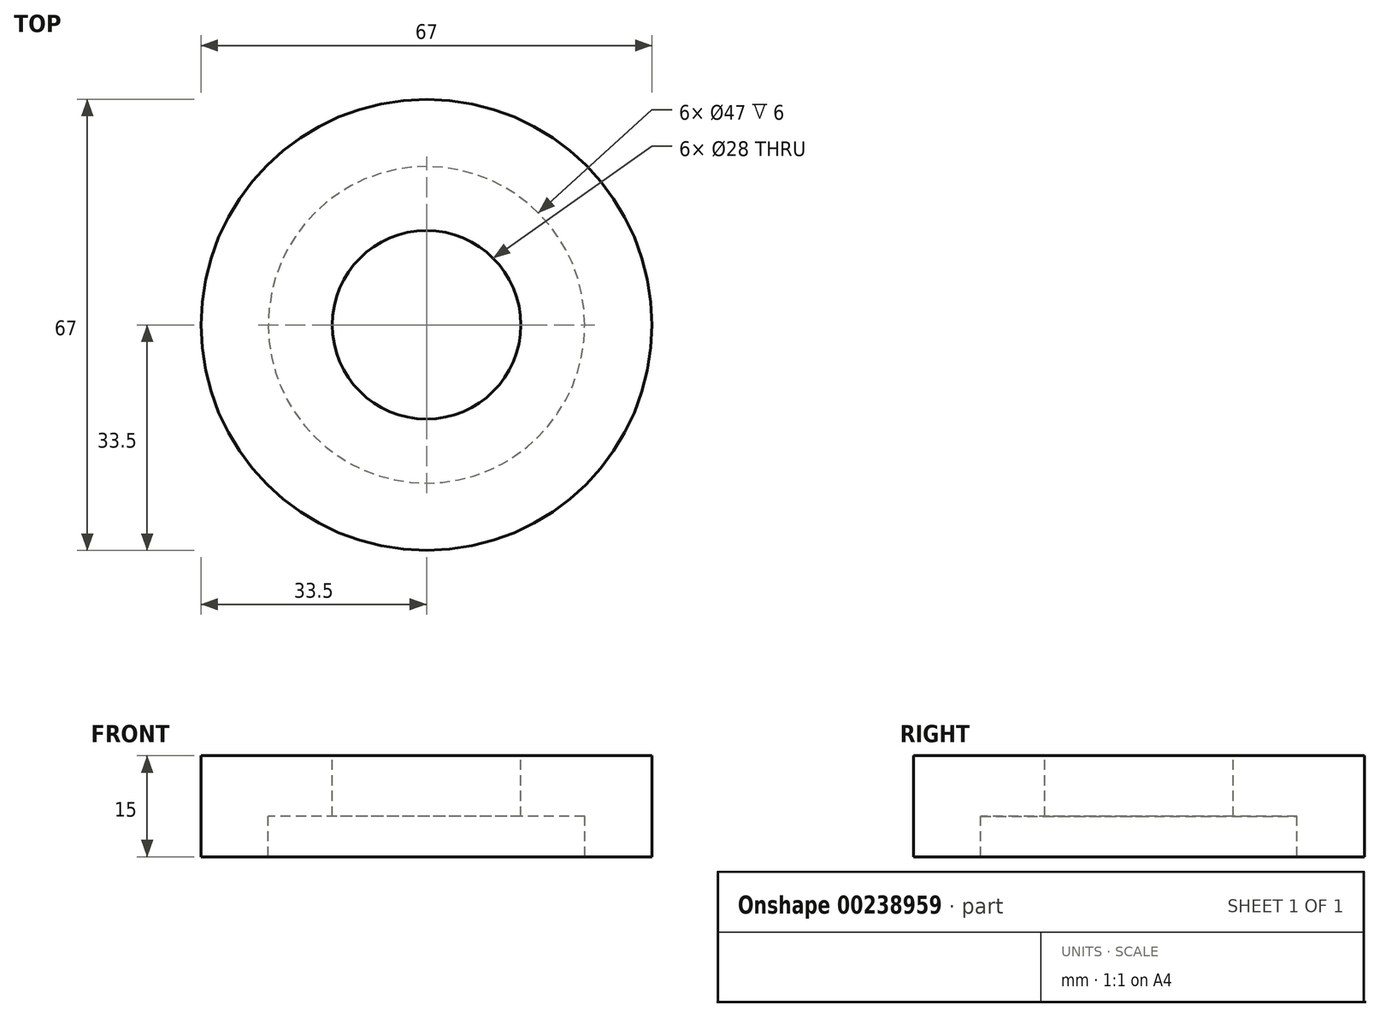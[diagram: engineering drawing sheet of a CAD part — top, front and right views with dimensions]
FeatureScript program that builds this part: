
annotation { "Feature Type Name" : "Feature", "Feature Type Description" : "" }
export const myFeature = defineFeature(function(context is Context, id is Id, definition is map)
    precondition{}
    {
        {
            var Q0;
            Q0=qCreatedBy(makeId("Front.planeOp"),FACE);
            var sketch = newSketch(context, id + "F0", { "sketchPlane" : qUnion([Q0])});
            skLineSegment(sketch, "E0", {"start": v(0, 42.97) * mm, "end": v(0, -19.44) * mm, "construction": true});
            skLineSegment(sketch, "E1", {"start": v(-14, 22.58) * mm, "end": v(-14, 6) * mm});
            skLineSegment(sketch, "E2", {"start": v(-33.5, 40.25) * mm, "end": v(-33.5, 0) * mm});
            skLineSegment(sketch, "E3", {"start": v(-23.5, 6) * mm, "end": v(-14, 6) * mm});
            skLineSegment(sketch, "E4", {"start": v(-33.5, 15) * mm, "end": v(-14, 15) * mm});
            skLineSegment(sketch, "E5.trimOffspring", {"start": v(-23.5, 0) * mm, "end": v(-33.5, 0) * mm});
            skLineSegment(sketch, "E6.trimOffspring", {"start": v(-23.5, 6) * mm, "end": v(-23.5, 0) * mm});
            skPoint(sketch, "E7.start.orphan", {"position": v(-23.5, 22.58) * mm});
            skSolve(sketch);
        }
        {
            var Q0;
            {var subQ1=sQuery(id+"F0.wireOp",EDGE,"E3");Q0=makeQuery(id+"F0.imprint","IMPRINT",FACE,{"disambiguationData":[TD([[makeQuery(id+"F0.imprint","IMPRINT",EDGE,{"derivedFrom":subQ1}),1.0]])]});}
            var Q1;
            Q1=sQuery(id+"F0.wireOp",EDGE,"E0");
            revolve(context, id + "F1", {"entities" : qUnion([Q0]), "axis" : qUnion([Q1]), "revolveType" : RevolveType.FULL});
        }
    });
